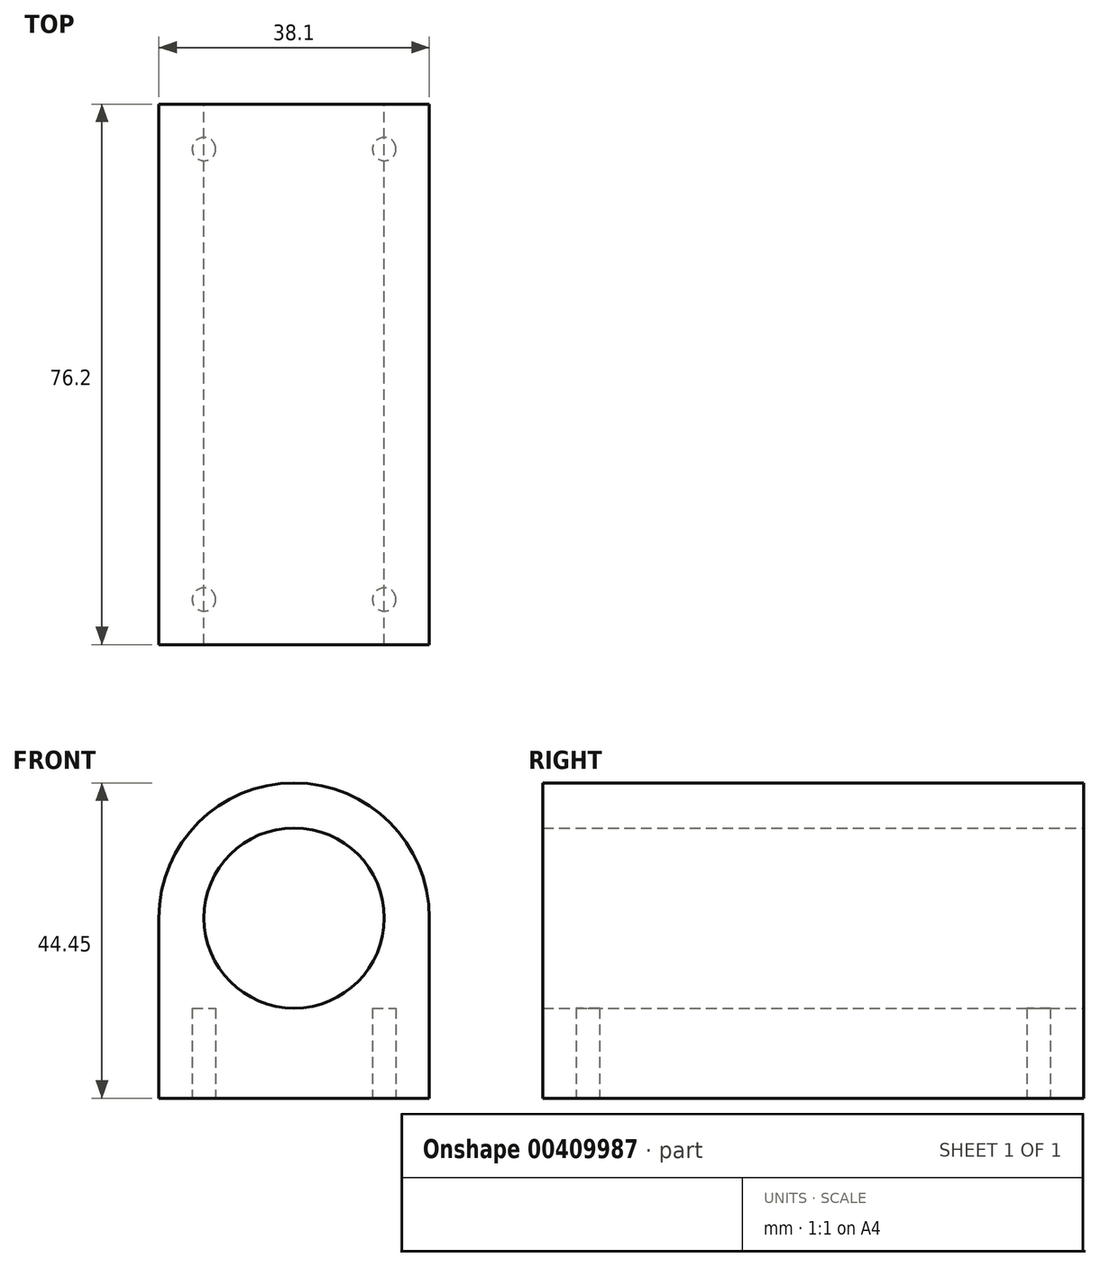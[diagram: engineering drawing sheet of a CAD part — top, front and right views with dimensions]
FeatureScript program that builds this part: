
annotation { "Feature Type Name" : "Feature", "Feature Type Description" : "" }
export const myFeature = defineFeature(function(context is Context, id is Id, definition is map)
    precondition{}
    {
        {
            var Q0;
            Q0=qCreatedBy(makeId("Front.planeOp"),FACE);
            var sketch = newSketch(context, id + "F0", { "sketchPlane" : qUnion([Q0])});
            skCircle(sketch, "E0", {"center": v(0, 0) * mm, "radius": 12.7 * mm});
            skArc(sketch, "E1", {"start": v(19.05, 0) * mm, "mid": v(0, 19.05) * mm, "end": v(-19.05, 0) * mm});
            skLineSegment(sketch, "E2", {"start": v(-19.05, 0) * mm, "end": v(-19.05, -25.4) * mm});
            skLineSegment(sketch, "E3", {"start": v(-19.05, -25.4) * mm, "end": v(19.05, -25.4) * mm});
            skLineSegment(sketch, "E4", {"start": v(19.05, -25.4) * mm, "end": v(19.05, 0) * mm});
            skSolve(sketch);
        }
        {
            var Q0;
            Q0 = qSketchRegion(id + "F0", true);
            extrude(context, id + "F1", {"entities" : qUnion([Q0]), "depth" : 76.2 * mm});
        }
        {
            var Q0;
            Q0=makeQuery(id+"F1.opExtrude","SWEPT_FACE",FACE,{"disambiguationData":[OSD([sQuery(id+"F0.wireOp",EDGE,"E3")])]});
            var sketch = newSketch(context, id + "F2", { "sketchPlane" : qUnion([Q0])});
            skLineSegment(sketch, "E5", {"start": v(-68.26, 38.1) * mm, "end": v(61.33, 38.1) * mm, "construction": true});
            skLineSegment(sketch, "E6.bottom", {"start": v(-12.7, 6.35) * mm, "end": v(12.7, 6.35) * mm, "construction": true});
            skLineSegment(sketch, "E6.top", {"start": v(-12.7, 69.85) * mm, "end": v(12.7, 69.85) * mm, "construction": true});
            skLineSegment(sketch, "E6.left", {"start": v(-12.7, 6.35) * mm, "end": v(-12.7, 69.85) * mm, "construction": true});
            skLineSegment(sketch, "E6.right", {"start": v(12.7, 6.35) * mm, "end": v(12.7, 69.85) * mm, "construction": true});
            skCircle(sketch, "E7", {"center": v(-12.7, 6.35) * mm, "radius": 1.65 * mm});
            skCircle(sketch, "E8.MirrorC", {"center": v(12.7, 6.35) * mm, "radius": 1.65 * mm});
            skCircle(sketch, "E9.MirrorC", {"center": v(-12.7, 69.85) * mm, "radius": 1.65 * mm});
            skCircle(sketch, "E10.MirrorC", {"center": v(12.7, 69.85) * mm, "radius": 1.65 * mm});
            skSolve(sketch);
        }
        {
            var Q0;
            Q0 = qSketchRegion(id + "F2", true);
            extrude(context, id + "F3", {"entities" : qUnion([Q0]), "operationType" : NewBodyOperationType.REMOVE, "oppositeDirection" : true, "depth" : 12.7 * mm});
        }
    });
